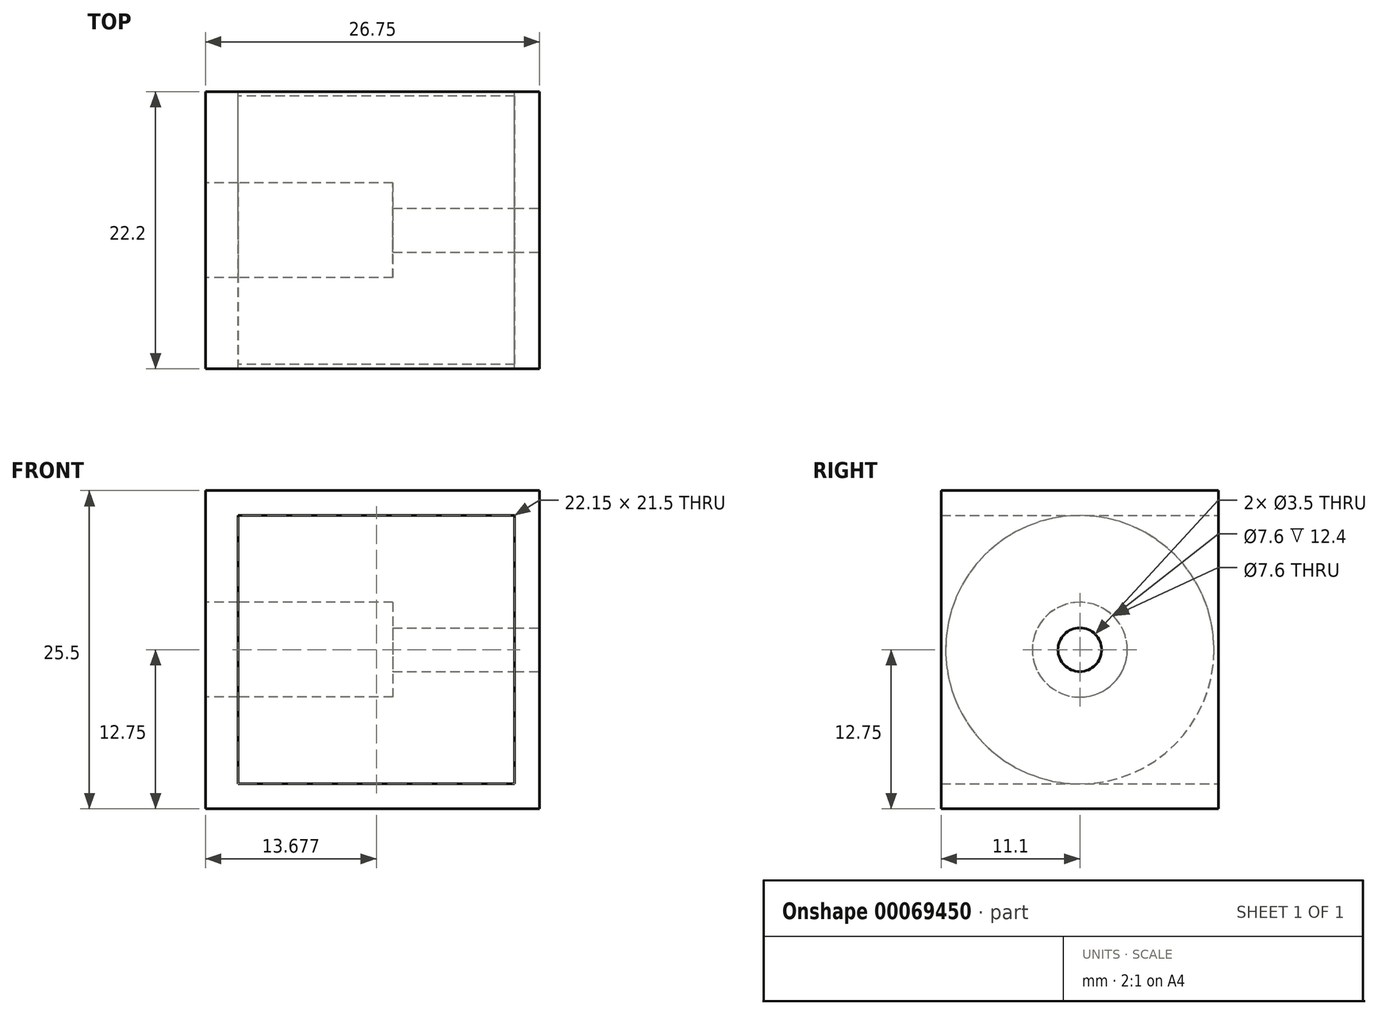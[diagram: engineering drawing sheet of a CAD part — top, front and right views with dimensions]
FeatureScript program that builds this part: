
annotation { "Feature Type Name" : "Feature", "Feature Type Description" : "" }
export const myFeature = defineFeature(function(context is Context, id is Id, definition is map)
    precondition{}
    {
        {
            var Q0;
            Q0=qCreatedBy(makeId("Front.planeOp"),FACE);
            var sketch = newSketch(context, id + "F0", { "sketchPlane" : qUnion([Q0])});
            skLineSegment(sketch, "E0", {"start": v(-49.13, 0) * mm, "end": v(-22.38, 0) * mm});
            skLineSegment(sketch, "E1.top", {"start": v(-49.13, 12.75) * mm, "end": v(-22.38, 12.75) * mm});
            skLineSegment(sketch, "E1.left", {"start": v(-49.13, 0) * mm, "end": v(-49.13, 12.75) * mm});
            skLineSegment(sketch, "E1.right", {"start": v(-22.38, 0) * mm, "end": v(-22.38, 12.75) * mm});
            skLineSegment(sketch, "E2.bottom", {"start": v(-46.53, 0) * mm, "end": v(-24.38, 0) * mm});
            skLineSegment(sketch, "E2.top", {"start": v(-46.53, 10.75) * mm, "end": v(-24.38, 10.75) * mm});
            skLineSegment(sketch, "E2.left", {"start": v(-46.53, 0) * mm, "end": v(-46.53, 10.75) * mm});
            skLineSegment(sketch, "E2.right", {"start": v(-24.38, 0) * mm, "end": v(-24.38, 10.75) * mm});
            skLineSegment(sketch, "E3.MirrorCS", {"start": v(-46.53, 0) * mm, "end": v(-46.53, -10.75) * mm});
            skLineSegment(sketch, "E4.MirrorCS", {"start": v(-49.13, 0) * mm, "end": v(-49.13, -12.75) * mm});
            skLineSegment(sketch, "E5.MirrorCS", {"start": v(-49.13, -12.75) * mm, "end": v(-22.38, -12.75) * mm});
            skLineSegment(sketch, "E6.MirrorCS", {"start": v(-46.53, -10.75) * mm, "end": v(-24.38, -10.75) * mm});
            skLineSegment(sketch, "E7.MirrorCS", {"start": v(-24.38, 0) * mm, "end": v(-24.38, -10.75) * mm});
            skLineSegment(sketch, "E8.MirrorCS", {"start": v(-22.38, 0) * mm, "end": v(-22.38, -12.75) * mm});
            skSolve(sketch);
        }
        {
            var Q0;
            Q0=makeQuery(id+"F0.imprint","IMPRINT",FACE,{"disambiguationData":[TD([[makeQuery(id+"F0.imprint","IMPRINT",EDGE,{"derivedFrom":sQuery(id+"F0.wireOp",EDGE,"E1.top")}),-1.0]])]});
            var Q1;
            {var subQ1=sQuery(id+"F0.wireOp",EDGE,"E3.MirrorCS");Q1=makeQuery(id+"F0.imprint","IMPRINT",FACE,{"disambiguationData":[TD([[makeQuery(id+"F0.imprint","IMPRINT",EDGE,{"derivedFrom":subQ1}),-1.0]])]});}
            extrude(context, id + "F1", {"entities" : qUnion([Q0, Q1]), "endBound" : BoundingType.SYMMETRIC, "depth" : 22.2 * mm});
        }
        {
            var Q0;
            Q0=makeQuery(id+"F1.opExtrude","SWEPT_FACE",FACE,{"disambiguationData":[OSD([sQuery(id+"F0.wireOp",EDGE,"E2.left"),sQuery(id+"F0.wireOp",EDGE,"E3.MirrorCS")])]});
            var sketch = newSketch(context, id + "F2", { "sketchPlane" : qUnion([Q0])});
            skCircle(sketch, "E9", {"center": v(0, 0) * mm, "radius": 10.75 * mm});
            skSolve(sketch);
        }
        {
            var Q0;
            {var subQ0=sQuery(id+"F2.wireOp",EDGE,"E9");var subQ1=makeQuery(id+"F2.imprint","INTERSECT",VERTEX,{"derivedFrom":[makeQuery(id+"F1.opExtrude","SWEPT_EDGE",EDGE,{"disambiguationData":[OSD([sQuery(id+"F0.wireOp",EDGE,"E2.top"),sQuery(id+"F0.wireOp",EDGE,"E2.left")])]}),subQ0]});Q0=makeQuery(id+"F2.imprint","IMPRINT",FACE,{"disambiguationData":[TD([[makeQuery(id+"F2.imprint","IMPRINT",EDGE,{"disambiguationData":[TD([[subQ1,-1.0]])],"derivedFrom":subQ0}),1.0]])]});}
            extrude(context, id + "F3", {"entities" : qUnion([Q0]), "endBound" : BoundingType.UP_TO_NEXT, "depth" : 25 * mm});
        }
        {
            var Q0;
            Q0=makeQuery(id+"F1.opExtrude","SWEPT_FACE",FACE,{"disambiguationData":[OSD([sQuery(id+"F0.wireOp",EDGE,"E1.right"),sQuery(id+"F0.wireOp",EDGE,"E8.MirrorCS")])]});
            var sketch = newSketch(context, id + "F4", { "sketchPlane" : qUnion([Q0])});
            skCircle(sketch, "E10", {"center": v(0, 0) * mm, "radius": 1.75 * mm});
            skSolve(sketch);
        }
        {
            var Q0;
            Q0 = qSketchRegion(id + "F4", true);
            var Q1;
            Q1=makeQuery(id+"F1.opExtrude","SWEPT_FACE",FACE,{"disambiguationData":[OSD([sQuery(id+"F0.wireOp",EDGE,"E1.left"),sQuery(id+"F0.wireOp",EDGE,"E4.MirrorCS")])]});
            extrude(context, id + "F5", {"entities" : qUnion([Q0]), "operationType" : NewBodyOperationType.REMOVE, "endBound" : BoundingType.UP_TO_SURFACE, "oppositeDirection" : true, "endBoundEntityFace" : qUnion([Q1]), "depth" : 25 * mm});
        }
        {
            var Q0;
            Q0=makeQuery(id+"F1.opExtrude","SWEPT_FACE",FACE,{"disambiguationData":[OSD([sQuery(id+"F0.wireOp",EDGE,"E1.left"),sQuery(id+"F0.wireOp",EDGE,"E4.MirrorCS")])]});
            var sketch = newSketch(context, id + "F6", { "sketchPlane" : qUnion([Q0])});
            skCircle(sketch, "E11", {"center": v(0, 0) * mm, "radius": 3.8 * mm});
            skSolve(sketch);
        }
        {
            var Q0;
            Q0 = qSketchRegion(id + "F6", true);
            var Q1;
            Q1=makeQuery(id+"F6.imprint","IMPRINT",FACE,{"disambiguationData":[TD([[makeQuery(id+"F6.imprint","IMPRINT",EDGE,{"derivedFrom":sQuery(id+"F6.wireOp",EDGE,"E11")}),1.0]])]});
            extrude(context, id + "F7", {"entities" : qUnion([Q0, Q1]), "operationType" : NewBodyOperationType.REMOVE, "oppositeDirection" : true, "depth" : 15 * mm});
        }
    });
